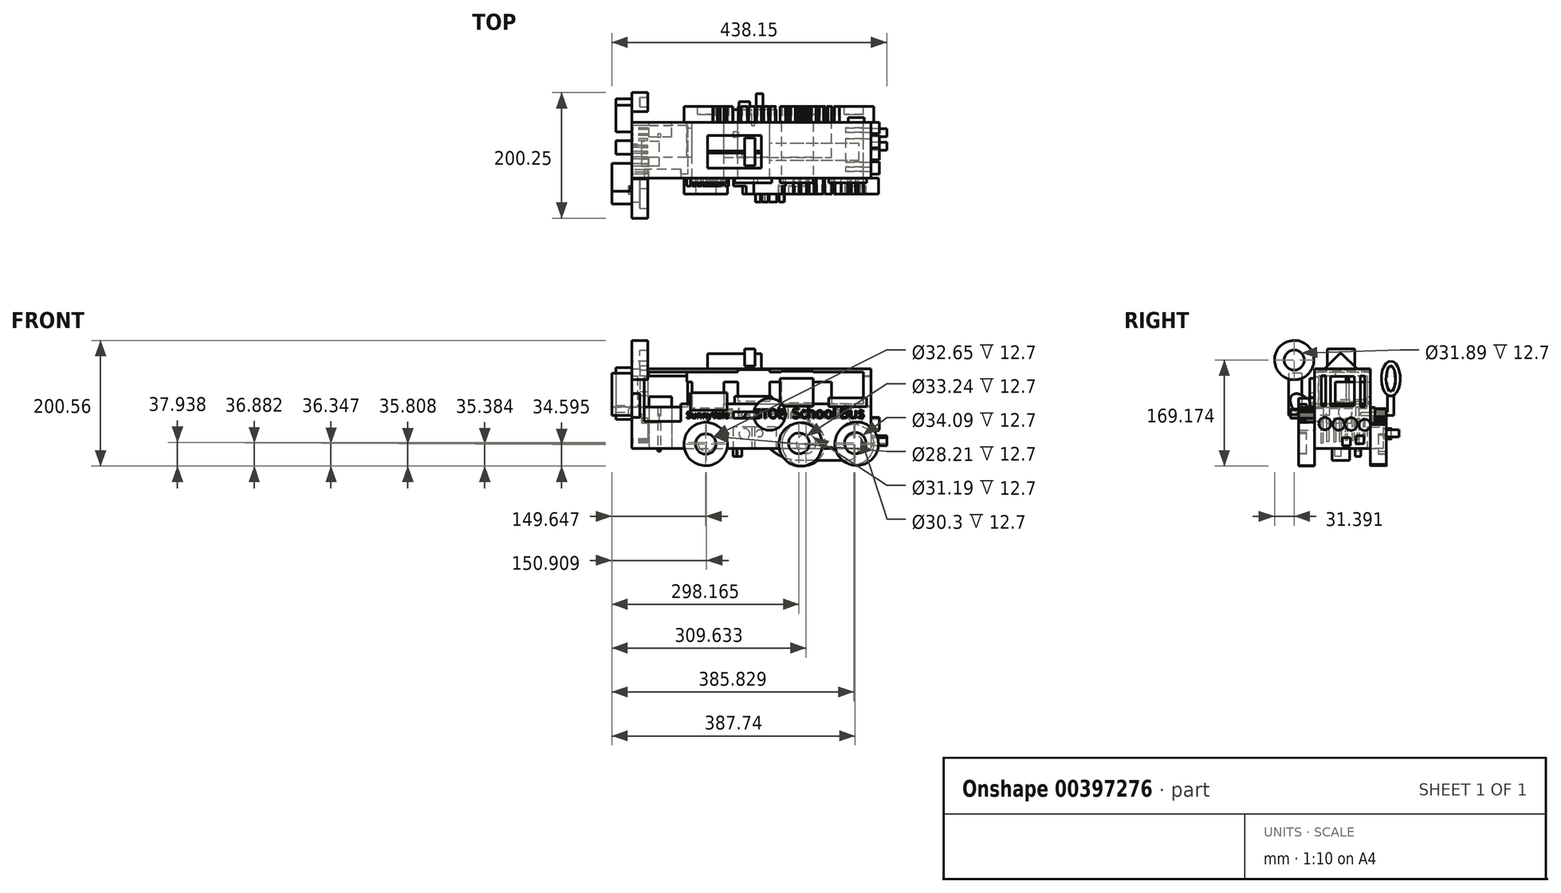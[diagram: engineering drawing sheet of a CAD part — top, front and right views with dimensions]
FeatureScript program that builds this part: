
annotation { "Feature Type Name" : "Feature", "Feature Type Description" : "" }
export const myFeature = defineFeature(function(context is Context, id is Id, definition is map)
    precondition{}
    {
        {
            var Q0;
            Q0=qCreatedBy(makeId("Front.planeOp"),FACE);
            var sketch = newSketch(context, id + "F0", { "sketchPlane" : qUnion([Q0])});
            skLineSegment(sketch, "E0.bottom", {"start": v(-219.61, 78.33) * mm, "end": v(161.39, 78.33) * mm});
            skLineSegment(sketch, "E0.top", {"start": v(-219.61, -48.19) * mm, "end": v(161.39, -48.19) * mm});
            skLineSegment(sketch, "E0.left", {"start": v(-219.61, 78.33) * mm, "end": v(-219.61, -48.19) * mm});
            skLineSegment(sketch, "E0.right", {"start": v(161.39, 78.33) * mm, "end": v(161.39, -48.19) * mm});
            skSolve(sketch);
        }
        {
            var Q0;
            Q0 = qSketchRegion(id + "F0", true);
            extrude(context, id + "F1", {"entities" : qUnion([Q0]), "depth" : 88.9 * mm});
        }
        {
            var Q0;
            Q0=makeQuery(id+"F1.opExtrude","CAP_FACE",FACE,{"disambiguationData":[OSD([sQuery(id+"F0.wireOp",EDGE,"E0.bottom"),sQuery(id+"F0.wireOp",EDGE,"E0.top"),sQuery(id+"F0.wireOp",EDGE,"E0.left"),sQuery(id+"F0.wireOp",EDGE,"E0.right")])],"isStart":true});
            var sketch = newSketch(context, id + "F2", { "sketchPlane" : qUnion([Q0])});
            skLineSegment(sketch, "E1.bottom", {"start": v(-149.58, 73.3) * mm, "end": v(-98.78, 73.3) * mm});
            skLineSegment(sketch, "E1.top", {"start": v(-149.58, 22.5) * mm, "end": v(-98.78, 22.5) * mm});
            skLineSegment(sketch, "E1.left", {"start": v(-149.58, 73.3) * mm, "end": v(-149.58, 22.5) * mm});
            skLineSegment(sketch, "E1.right", {"start": v(-98.78, 73.3) * mm, "end": v(-98.78, 22.5) * mm});
            skSolve(sketch);
        }
        {
            var Q0;
            Q0 = qSketchRegion(id + "F2", true);
            extrude(context, id + "F3", {"entities" : qUnion([Q0]), "operationType" : NewBodyOperationType.REMOVE, "oppositeDirection" : true, "depth" : 127 * mm});
        }
        {
            var Q0;
            Q0=makeQuery(id+"F1.opExtrude","CAP_FACE",FACE,{"disambiguationData":[OSD([sQuery(id+"F0.wireOp",EDGE,"E0.bottom"),sQuery(id+"F0.wireOp",EDGE,"E0.top"),sQuery(id+"F0.wireOp",EDGE,"E0.left"),sQuery(id+"F0.wireOp",EDGE,"E0.right")])],"isStart":false});
            var sketch = newSketch(context, id + "F4", { "sketchPlane" : qUnion([Q0])});
            skLineSegment(sketch, "E2.bottom", {"start": v(18.54, 74.81) * mm, "end": v(69.34, 74.81) * mm});
            skLineSegment(sketch, "E2.top", {"start": v(18.54, 24.01) * mm, "end": v(69.34, 24.01) * mm});
            skLineSegment(sketch, "E2.left", {"start": v(18.54, 74.81) * mm, "end": v(18.54, 24.01) * mm});
            skLineSegment(sketch, "E2.right", {"start": v(69.34, 74.81) * mm, "end": v(69.34, 24.01) * mm});
            skSolve(sketch);
        }
        {
            var Q0;
            Q0 = qSketchRegion(id + "F4", true);
            extrude(context, id + "F5", {"entities" : qUnion([Q0]), "operationType" : NewBodyOperationType.REMOVE, "oppositeDirection" : true, "depth" : 125.48 * mm});
        }
        {
            var Q0;
            Q0=makeQuery(id+"F1.opExtrude","CAP_FACE",FACE,{"disambiguationData":[OSD([sQuery(id+"F0.wireOp",EDGE,"E0.bottom"),sQuery(id+"F0.wireOp",EDGE,"E0.top"),sQuery(id+"F0.wireOp",EDGE,"E0.left"),sQuery(id+"F0.wireOp",EDGE,"E0.right")])],"isStart":true});
            var sketch = newSketch(context, id + "F6", { "sketchPlane" : qUnion([Q0])});
            skLineSegment(sketch, "E3.bottom", {"start": v(0, 76.96) * mm, "end": v(50.8, 76.96) * mm});
            skLineSegment(sketch, "E3.top", {"start": v(0, 26.16) * mm, "end": v(50.8, 26.16) * mm});
            skLineSegment(sketch, "E3.left", {"start": v(0, 76.96) * mm, "end": v(0, 26.16) * mm});
            skLineSegment(sketch, "E3.right", {"start": v(50.8, 76.96) * mm, "end": v(50.8, 26.16) * mm});
            skSolve(sketch);
        }
        {
            var Q0;
            Q0 = qSketchRegion(id + "F6", true);
            extrude(context, id + "F7", {"entities" : qUnion([Q0]), "operationType" : NewBodyOperationType.REMOVE, "oppositeDirection" : true, "depth" : 353.06 * mm});
        }
        {
            var Q0;
            Q0=makeQuery(id+"F1.opExtrude","CAP_FACE",FACE,{"disambiguationData":[OSD([sQuery(id+"F0.wireOp",EDGE,"E0.bottom"),sQuery(id+"F0.wireOp",EDGE,"E0.top"),sQuery(id+"F0.wireOp",EDGE,"E0.left"),sQuery(id+"F0.wireOp",EDGE,"E0.right")])],"isStart":true});
            var sketch = newSketch(context, id + "F8", { "sketchPlane" : qUnion([Q0])});
            skLineSegment(sketch, "E4.bottom", {"start": v(72.64, 66.26) * mm, "end": v(123.44, 66.26) * mm});
            skLineSegment(sketch, "E4.top", {"start": v(72.64, 15.46) * mm, "end": v(123.44, 15.46) * mm});
            skLineSegment(sketch, "E4.left", {"start": v(72.64, 66.26) * mm, "end": v(72.64, 15.46) * mm});
            skLineSegment(sketch, "E4.right", {"start": v(123.44, 66.26) * mm, "end": v(123.44, 15.46) * mm});
            skSolve(sketch);
        }
        {
            var Q0;
            Q0 = qSketchRegion(id + "F8", true);
            extrude(context, id + "F9", {"entities" : qUnion([Q0]), "operationType" : NewBodyOperationType.REMOVE, "oppositeDirection" : true, "depth" : 349 * mm});
        }
        {
            var Q0;
            Q0=makeQuery(id+"F1.opExtrude","CAP_FACE",FACE,{"disambiguationData":[OSD([sQuery(id+"F0.wireOp",EDGE,"E0.bottom"),sQuery(id+"F0.wireOp",EDGE,"E0.top"),sQuery(id+"F0.wireOp",EDGE,"E0.left"),sQuery(id+"F0.wireOp",EDGE,"E0.right")])],"isStart":true});
            var sketch = newSketch(context, id + "F10", { "sketchPlane" : qUnion([Q0])});
            skLineSegment(sketch, "E5.bottom", {"start": v(155.7, 34.18) * mm, "end": v(191.92, 34.18) * mm});
            skLineSegment(sketch, "E5.top", {"start": v(155.7, -48.19) * mm, "end": v(191.92, -48.19) * mm});
            skLineSegment(sketch, "E5.left", {"start": v(155.7, 34.18) * mm, "end": v(155.7, -48.19) * mm});
            skLineSegment(sketch, "E5.right", {"start": v(191.92, 34.18) * mm, "end": v(191.92, -48.19) * mm});
            skSolve(sketch);
        }
        {
            var Q0;
            Q0 = qSketchRegion(id + "F10", true);
            extrude(context, id + "F11", {"entities" : qUnion([Q0]), "operationType" : NewBodyOperationType.REMOVE, "oppositeDirection" : true, "depth" : 23.37 * mm});
        }
        {
            var Q0;
            Q0=makeQuery(id+"F1.opExtrude","SWEPT_FACE",FACE,{"disambiguationData":[OSD([sQuery(id+"F0.wireOp",EDGE,"E0.left")])]});
            var sketch = newSketch(context, id + "F12", { "sketchPlane" : qUnion([Q0])});
            skLineSegment(sketch, "E6.bottom", {"start": v(5.3, 67.15) * mm, "end": v(82.5, 67.15) * mm});
            skLineSegment(sketch, "E6.top", {"start": v(5.3, 17.89) * mm, "end": v(82.5, 17.89) * mm});
            skLineSegment(sketch, "E6.left", {"start": v(5.3, 67.15) * mm, "end": v(5.3, 17.89) * mm});
            skLineSegment(sketch, "E6.right", {"start": v(82.5, 67.15) * mm, "end": v(82.5, 17.89) * mm});
            skSolve(sketch);
        }
        {
            var Q0;
            Q0 = qSketchRegion(id + "F12", true);
            extrude(context, id + "F13", {"entities" : qUnion([Q0]), "operationType" : NewBodyOperationType.REMOVE, "oppositeDirection" : true, "depth" : 88.9 * mm});
        }
        {
            var Q0;
            Q0=makeQuery(id+"F1.opExtrude","CAP_FACE",FACE,{"disambiguationData":[OSD([sQuery(id+"F0.wireOp",EDGE,"E0.bottom"),sQuery(id+"F0.wireOp",EDGE,"E0.top"),sQuery(id+"F0.wireOp",EDGE,"E0.left"),sQuery(id+"F0.wireOp",EDGE,"E0.right")])],"isStart":true});
            var sketch = newSketch(context, id + "F14", { "sketchPlane" : qUnion([Q0])});
            skCircle(sketch, "E7", {"center": v(-134.47, -42.1) * mm, "radius": 31.77 * mm});
            skSolve(sketch);
        }
        {
            var Q0;
            Q0 = qSketchRegion(id + "F14", true);
            extrude(context, id + "F15", {"entities" : qUnion([Q0]), "operationType" : NewBodyOperationType.ADD, "depth" : 25.4 * mm});
        }
        {
            var Q0;
            Q0=makeQuery(id+"F1.opExtrude","CAP_FACE",FACE,{"disambiguationData":[OSD([sQuery(id+"F0.wireOp",EDGE,"E0.bottom"),sQuery(id+"F0.wireOp",EDGE,"E0.top"),sQuery(id+"F0.wireOp",EDGE,"E0.left"),sQuery(id+"F0.wireOp",EDGE,"E0.right")])],"isStart":true});
            var sketch = newSketch(context, id + "F16", { "sketchPlane" : qUnion([Q0])});
            skCircle(sketch, "E8", {"center": v(-54.26, -41.2) * mm, "radius": 34.6 * mm});
            skSolve(sketch);
        }
        {
            var Q0;
            Q0 = qSketchRegion(id + "F16", true);
            extrude(context, id + "F17", {"entities" : qUnion([Q0]), "operationType" : NewBodyOperationType.ADD, "depth" : 25.4 * mm});
        }
        {
            var Q0;
            Q0=makeQuery(id+"F1.opExtrude","CAP_FACE",FACE,{"disambiguationData":[OSD([sQuery(id+"F0.wireOp",EDGE,"E0.bottom"),sQuery(id+"F0.wireOp",EDGE,"E0.top"),sQuery(id+"F0.wireOp",EDGE,"E0.left"),sQuery(id+"F0.wireOp",EDGE,"E0.right")])],"isStart":true});
            var sketch = newSketch(context, id + "F18", { "sketchPlane" : qUnion([Q0])});
            skCircle(sketch, "E9", {"center": v(101.85, -41.13) * mm, "radius": 34.6 * mm});
            skSolve(sketch);
        }
        {
            var Q0;
            Q0 = qSketchRegion(id + "F18", true);
            extrude(context, id + "F19", {"entities" : qUnion([Q0]), "operationType" : NewBodyOperationType.ADD, "depth" : 25.4 * mm});
        }
        {
            var Q0;
            Q0=makeQuery(id+"F4.imprint","IMPRINT",FACE,{"disambiguationData":[TD([[makeQuery(id+"F4.imprint","IMPRINT",EDGE,{"derivedFrom":sQuery(id+"F4.wireOp",EDGE,"E2.bottom")}),1.0]])]});
            var sketch = newSketch(context, id + "F20", { "sketchPlane" : qUnion([Q0])});
            skCircle(sketch, "E10", {"center": v(138.8, -40.97) * mm, "radius": 34.6 * mm});
            skSolve(sketch);
        }
        {
            var Q0;
            Q0 = qSketchRegion(id + "F20", true);
            extrude(context, id + "F21", {"entities" : qUnion([Q0]), "operationType" : NewBodyOperationType.ADD, "depth" : 25.4 * mm});
        }
        {
            var Q0;
            Q0=makeQuery(id+"F4.imprint","IMPRINT",FACE,{"disambiguationData":[TD([[makeQuery(id+"F4.imprint","IMPRINT",EDGE,{"derivedFrom":sQuery(id+"F4.wireOp",EDGE,"E2.bottom")}),1.0]])]});
            var sketch = newSketch(context, id + "F22", { "sketchPlane" : qUnion([Q0])});
            skCircle(sketch, "E11", {"center": v(49.35, -42.1) * mm, "radius": 34.6 * mm});
            skSolve(sketch);
        }
        {
            var Q0;
            Q0 = qSketchRegion(id + "F22", true);
            extrude(context, id + "F23", {"entities" : qUnion([Q0]), "operationType" : NewBodyOperationType.ADD, "depth" : 25.4 * mm});
        }
        {
            var Q0;
            Q0=makeQuery(id+"F4.imprint","IMPRINT",FACE,{"disambiguationData":[TD([[makeQuery(id+"F4.imprint","IMPRINT",EDGE,{"derivedFrom":sQuery(id+"F4.wireOp",EDGE,"E2.bottom")}),1.0]])]});
            var sketch = newSketch(context, id + "F24", { "sketchPlane" : qUnion([Q0])});
            skCircle(sketch, "E12", {"center": v(-101.71, -41.32) * mm, "radius": 34.6 * mm});
            skSolve(sketch);
        }
        {
            var Q0;
            Q0 = qSketchRegion(id + "F24", true);
            extrude(context, id + "F25", {"entities" : qUnion([Q0]), "operationType" : NewBodyOperationType.ADD, "depth" : 25.4 * mm});
        }
        {
            var Q0;
            Q0=makeQuery(id+"F4.imprint","IMPRINT",FACE,{"disambiguationData":[TD([[makeQuery(id+"F4.imprint","IMPRINT",EDGE,{"derivedFrom":sQuery(id+"F4.wireOp",EDGE,"E2.bottom")}),1.0]])]});
            var sketch = newSketch(context, id + "F26", { "sketchPlane" : qUnion([Q0])});
            skLineSegment(sketch, "E13.bottom", {"start": v(-199.74, 65.16) * mm, "end": v(-141.38, 65.16) * mm});
            skLineSegment(sketch, "E13.top", {"start": v(-199.74, -5.59) * mm, "end": v(-141.38, -5.59) * mm});
            skLineSegment(sketch, "E13.left", {"start": v(-199.74, 65.16) * mm, "end": v(-199.74, -5.59) * mm});
            skLineSegment(sketch, "E13.right", {"start": v(-141.38, 65.16) * mm, "end": v(-141.38, -5.59) * mm});
            skSolve(sketch);
        }
        {
            var Q0;
            Q0 = qSketchRegion(id + "F26", true);
            extrude(context, id + "F27", {"entities" : qUnion([Q0]), "operationType" : NewBodyOperationType.REMOVE, "oppositeDirection" : true, "depth" : 13.97 * mm});
        }
        {
            var Q0;
            Q0=makeQuery(id+"F1.opExtrude","SWEPT_FACE",FACE,{"disambiguationData":[OSD([sQuery(id+"F0.wireOp",EDGE,"E0.bottom")])]});
            var sketch = newSketch(context, id + "F28", { "sketchPlane" : qUnion([Q0])});
            skLineSegment(sketch, "E14.bottom", {"start": v(-99.07, -74.11) * mm, "end": v(-13, -74.11) * mm});
            skLineSegment(sketch, "E14.top", {"start": v(-99.07, -20.3) * mm, "end": v(-13, -20.3) * mm});
            skLineSegment(sketch, "E14.left", {"start": v(-99.07, -74.11) * mm, "end": v(-99.07, -20.3) * mm});
            skLineSegment(sketch, "E14.right", {"start": v(-13, -74.11) * mm, "end": v(-13, -20.3) * mm});
            skSolve(sketch);
        }
        {
            var Q0;
            Q0 = qSketchRegion(id + "F28", true);
            extrude(context, id + "F29", {"entities" : qUnion([Q0]), "operationType" : NewBodyOperationType.ADD, "depth" : 24.64 * mm});
        }
        {
            var Q0;
            Q0=makeQuery(id+"F29.opExtrude","CAP_FACE",FACE,{"disambiguationData":[OSD([sQuery(id+"F28.wireOp",EDGE,"E14.bottom"),sQuery(id+"F28.wireOp",EDGE,"E14.top"),sQuery(id+"F28.wireOp",EDGE,"E14.left"),sQuery(id+"F28.wireOp",EDGE,"E14.right")])],"isStart":false});
            var sketch = newSketch(context, id + "F30", { "sketchPlane" : qUnion([Q0])});
            skLineSegment(sketch, "E15.bottom", {"start": v(-39.87, -68.95) * mm, "end": v(-23.5, -68.95) * mm});
            skLineSegment(sketch, "E15.top", {"start": v(-39.87, -24.8) * mm, "end": v(-23.5, -24.8) * mm});
            skLineSegment(sketch, "E15.left", {"start": v(-39.87, -68.95) * mm, "end": v(-39.87, -24.8) * mm});
            skLineSegment(sketch, "E15.right", {"start": v(-23.5, -68.95) * mm, "end": v(-23.5, -24.8) * mm});
            skSolve(sketch);
        }
        {
            var Q0;
            Q0 = qSketchRegion(id + "F30", true);
            extrude(context, id + "F31", {"entities" : qUnion([Q0]), "operationType" : NewBodyOperationType.ADD, "depth" : 7.62 * mm});
        }
        {
            var Q0;
            Q0=makeQuery(id+"F1.opExtrude","SWEPT_FACE",FACE,{"disambiguationData":[OSD([sQuery(id+"F0.wireOp",EDGE,"E0.right")])]});
            var sketch = newSketch(context, id + "F32", { "sketchPlane" : qUnion([Q0])});
            skLineSegment(sketch, "E16.bottom", {"start": v(-22.79, -27.9) * mm, "end": v(-10.09, -27.9) * mm});
            skLineSegment(sketch, "E16.top", {"start": v(-22.79, -40.6) * mm, "end": v(-10.09, -40.6) * mm});
            skLineSegment(sketch, "E16.left", {"start": v(-22.79, -27.9) * mm, "end": v(-22.79, -40.6) * mm});
            skLineSegment(sketch, "E16.right", {"start": v(-10.09, -27.9) * mm, "end": v(-10.09, -40.6) * mm});
            skSolve(sketch);
        }
        {
            var Q0;
            Q0 = qSketchRegion(id + "F32", true);
            extrude(context, id + "F33", {"entities" : qUnion([Q0]), "operationType" : NewBodyOperationType.ADD, "depth" : 25.4 * mm});
        }
        {
            var Q0;
            Q0=makeQuery(id+"F1.opExtrude","SWEPT_FACE",FACE,{"disambiguationData":[OSD([sQuery(id+"F0.wireOp",EDGE,"E0.right")])]});
            var sketch = newSketch(context, id + "F34", { "sketchPlane" : qUnion([Q0])});
            skPoint(sketch, "E17.firstSnap0", {"position": v(-44.45, -48.19) * mm});
            skLineSegment(sketch, "E17.bottom", {"start": v(-44.45, -31.5) * mm, "end": v(-31.75, -31.5) * mm});
            skLineSegment(sketch, "E17.top", {"start": v(-44.45, -44.2) * mm, "end": v(-31.75, -44.2) * mm});
            skLineSegment(sketch, "E17.left", {"start": v(-44.45, -31.5) * mm, "end": v(-44.45, -44.2) * mm});
            skLineSegment(sketch, "E17.right", {"start": v(-31.75, -31.5) * mm, "end": v(-31.75, -44.2) * mm});
            skSolve(sketch);
        }
        {
            var Q0;
            Q0 = qSketchRegion(id + "F34", true);
            extrude(context, id + "F35", {"entities" : qUnion([Q0]), "operationType" : NewBodyOperationType.ADD, "depth" : 25.4 * mm});
        }
        {
            var Q0;
            Q0=makeQuery(id+"F13.boolean.opBoolean","COPY",FACE,{"derivedFrom":makeQuery(id+"F13.opExtrude","CAP_FACE",FACE,{"disambiguationData":[OSD([sQuery(id+"F12.wireOp",EDGE,"E6.bottom"),sQuery(id+"F12.wireOp",EDGE,"E6.top"),sQuery(id+"F12.wireOp",EDGE,"E6.left"),sQuery(id+"F12.wireOp",EDGE,"E6.right")])],"isStart":false})});
            var sketch = newSketch(context, id + "F36", { "sketchPlane" : qUnion([Q0])});
            skLineSegment(sketch, "E18.bottom", {"start": v(9.47, 63.82) * mm, "end": v(71.4, 63.82) * mm});
            skLineSegment(sketch, "E18.top", {"start": v(9.47, 29.22) * mm, "end": v(71.4, 29.22) * mm});
            skLineSegment(sketch, "E18.left", {"start": v(9.47, 63.82) * mm, "end": v(9.47, 29.22) * mm});
            skLineSegment(sketch, "E18.right", {"start": v(71.4, 63.82) * mm, "end": v(71.4, 29.22) * mm});
            skSolve(sketch);
        }
        {
            var Q0;
            Q0 = qSketchRegion(id + "F36", true);
            extrude(context, id + "F37", {"entities" : qUnion([Q0]), "operationType" : NewBodyOperationType.REMOVE, "oppositeDirection" : true, "depth" : 25.4 * mm});
        }
        {
            var Q0;
            Q0=makeQuery(id+"F11.boolean.opBoolean","COPY",FACE,{"derivedFrom":makeQuery(id+"F11.opExtrude","CAP_FACE",FACE,{"disambiguationData":[OSD([sQuery(id+"F10.wireOp",EDGE,"E5.bottom"),sQuery(id+"F10.wireOp",EDGE,"E5.top"),sQuery(id+"F10.wireOp",EDGE,"E5.left"),sQuery(id+"F10.wireOp",EDGE,"E5.right")])],"isStart":false})});
            var sketch = newSketch(context, id + "F38", { "sketchPlane" : qUnion([Q0])});
            skLineSegment(sketch, "E19.bottom", {"start": v(173.8, 17.89) * mm, "end": v(178.4, 17.89) * mm});
            skLineSegment(sketch, "E19.top", {"start": v(173.8, -53.03) * mm, "end": v(178.4, -53.03) * mm});
            skLineSegment(sketch, "E19.left", {"start": v(173.8, 17.89) * mm, "end": v(173.8, -53.03) * mm});
            skLineSegment(sketch, "E19.right", {"start": v(178.4, 17.89) * mm, "end": v(178.4, -53.03) * mm});
            skSolve(sketch);
        }
        {
            var Q0;
            Q0 = qSketchRegion(id + "F38", true);
            extrude(context, id + "F39", {"entities" : qUnion([Q0]), "operationType" : NewBodyOperationType.ADD, "depth" : 5.08 * mm});
        }
        {
            var Q0;
            Q0=makeQuery(id+"F1.opExtrude","SWEPT_FACE",FACE,{"disambiguationData":[OSD([sQuery(id+"F0.wireOp",EDGE,"E0.left")])]});
            var sketch = newSketch(context, id + "F40", { "sketchPlane" : qUnion([Q0])});
            skLineSegment(sketch, "E20.bottom", {"start": v(34.5, 72.23) * mm, "end": v(38.68, 72.23) * mm});
            skLineSegment(sketch, "E20.top", {"start": v(34.5, 11.97) * mm, "end": v(38.68, 11.97) * mm});
            skLineSegment(sketch, "E20.left", {"start": v(34.5, 72.23) * mm, "end": v(34.5, 11.97) * mm});
            skLineSegment(sketch, "E20.right", {"start": v(38.68, 72.23) * mm, "end": v(38.68, 11.97) * mm});
            skSolve(sketch);
        }
        {
            var Q0;
            Q0 = qSketchRegion(id + "F40", true);
            extrude(context, id + "F41", {"entities" : qUnion([Q0]), "operationType" : NewBodyOperationType.ADD, "oppositeDirection" : true, "depth" : 9.14 * mm});
        }
        {
            var Q0;
            Q0=makeQuery(id+"F4.imprint","IMPRINT",FACE,{"disambiguationData":[TD([[makeQuery(id+"F4.imprint","IMPRINT",EDGE,{"derivedFrom":sQuery(id+"F4.wireOp",EDGE,"E2.bottom")}),1.0]])]});
            var sketch = newSketch(context, id + "F42", { "sketchPlane" : qUnion([Q0])});
            skLineSegment(sketch, "E21.bottom", {"start": v(-57.35, 0) * mm, "end": v(-25.01, 0) * mm});
            skLineSegment(sketch, "E21.top", {"start": v(-57.35, 9.97) * mm, "end": v(-25.01, 9.97) * mm});
            skLineSegment(sketch, "E21.left", {"start": v(-57.35, 0) * mm, "end": v(-57.35, 9.97) * mm});
            skLineSegment(sketch, "E21.right", {"start": v(-25.01, 0) * mm, "end": v(-25.01, 9.97) * mm});
            skSolve(sketch);
        }
        {
            var Q0;
            Q0 = qSketchRegion(id + "F42", true);
            extrude(context, id + "F43", {"entities" : qUnion([Q0]), "operationType" : NewBodyOperationType.ADD, "depth" : 25.4 * mm});
        }
        {
            var Q0;
            Q0=makeQuery(id+"F4.imprint","IMPRINT",FACE,{"disambiguationData":[TD([[makeQuery(id+"F4.imprint","IMPRINT",EDGE,{"derivedFrom":sQuery(id+"F4.wireOp",EDGE,"E2.bottom")}),1.0]])]});
            var sketch = newSketch(context, id + "F44", { "sketchPlane" : qUnion([Q0])});
            skCircle(sketch, "E22", {"center": v(0, 6.06) * mm, "radius": 25.45 * mm});
            skSolve(sketch);
        }
        {
            var Q0;
            Q0 = qSketchRegion(id + "F44", true);
            extrude(context, id + "F45", {"entities" : qUnion([Q0]), "operationType" : NewBodyOperationType.ADD, "depth" : 25.4 * mm});
        }
        {
            var Q0;
            Q0=makeQuery(id+"F41.boolean.opBoolean","MERGE",FACE,{"derivedFrom":[makeQuery(id+"F1.opExtrude","SWEPT_FACE",FACE,{"disambiguationData":[OSD([sQuery(id+"F0.wireOp",EDGE,"E0.left")])]}),makeQuery(id+"F41.opExtrude","CAP_FACE",FACE,{"disambiguationData":[OSD([sQuery(id+"F40.wireOp",EDGE,"E20.bottom"),sQuery(id+"F40.wireOp",EDGE,"E20.top"),sQuery(id+"F40.wireOp",EDGE,"E20.left"),sQuery(id+"F40.wireOp",EDGE,"E20.right")])],"isStart":true})]});
            var sketch = newSketch(context, id + "F46", { "sketchPlane" : qUnion([Q0])});
            skLineSegment(sketch, "E23.bottom", {"start": v(15.22, 3.97) * mm, "end": v(-35.58, 3.97) * mm});
            skLineSegment(sketch, "E23.top", {"start": v(15.22, 9.05) * mm, "end": v(-35.58, 9.05) * mm});
            skLineSegment(sketch, "E23.left", {"start": v(15.22, 3.97) * mm, "end": v(15.22, 9.05) * mm});
            skLineSegment(sketch, "E23.right", {"start": v(-35.58, 3.97) * mm, "end": v(-35.58, 9.05) * mm});
            skSolve(sketch);
        }
        {
            var Q0;
            Q0 = qSketchRegion(id + "F46", true);
            extrude(context, id + "F47", {"entities" : qUnion([Q0]), "operationType" : NewBodyOperationType.ADD, "depth" : 25.4 * mm});
        }
        {
            var Q0;
            Q0=makeQuery(id+"F47.opExtrude","CAP_FACE",FACE,{"disambiguationData":[OSD([sQuery(id+"F46.wireOp",EDGE,"E23.bottom"),sQuery(id+"F46.wireOp",EDGE,"E23.top"),sQuery(id+"F46.wireOp",EDGE,"E23.left"),sQuery(id+"F46.wireOp",EDGE,"E23.right")])],"isStart":false});
            var sketch = newSketch(context, id + "F48", { "sketchPlane" : qUnion([Q0])});
            skLineSegment(sketch, "E24.bottom", {"start": v(-37.55, 80.17) * mm, "end": v(-27.39, 80.17) * mm});
            skLineSegment(sketch, "E24.top", {"start": v(-37.55, 3.97) * mm, "end": v(-27.39, 3.97) * mm});
            skLineSegment(sketch, "E24.left", {"start": v(-37.55, 80.17) * mm, "end": v(-37.55, 3.97) * mm});
            skLineSegment(sketch, "E24.right", {"start": v(-27.39, 80.17) * mm, "end": v(-27.39, 3.97) * mm});
            skSolve(sketch);
        }
        {
            var Q0;
            Q0 = qSketchRegion(id + "F48", true);
            extrude(context, id + "F49", {"entities" : qUnion([Q0]), "operationType" : NewBodyOperationType.ADD, "oppositeDirection" : true, "depth" : 25.4 * mm});
        }
        {
            var Q0;
            Q0=makeQuery(id+"F49.boolean.opBoolean","MERGE",FACE,{"derivedFrom":[makeQuery(id+"F47.opExtrude","CAP_FACE",FACE,{"disambiguationData":[OSD([sQuery(id+"F46.wireOp",EDGE,"E23.bottom"),sQuery(id+"F46.wireOp",EDGE,"E23.top"),sQuery(id+"F46.wireOp",EDGE,"E23.left"),sQuery(id+"F46.wireOp",EDGE,"E23.right")])],"isStart":true}),makeQuery(id+"F49.opExtrude","CAP_FACE",FACE,{"disambiguationData":[OSD([sQuery(id+"F48.wireOp",EDGE,"E24.bottom"),sQuery(id+"F48.wireOp",EDGE,"E24.top"),sQuery(id+"F48.wireOp",EDGE,"E24.left"),sQuery(id+"F48.wireOp",EDGE,"E24.right")])],"isStart":false})]});
            var sketch = newSketch(context, id + "F50", { "sketchPlane" : qUnion([Q0])});
            skEllipse(sketch, "E25", {"center": v(32.47, 62.95) * mm, "majorRadius": 27.83 * mm, "minorRadius": 15.03 * mm, "majorAxis": v(0, 1)});
            skPoint(sketch, "E25.centerSnap0", {"position": v(32.47, 80.17) * mm});
            skSolve(sketch);
        }
        {
            var Q0;
            Q0 = qSketchRegion(id + "F50", true);
            extrude(context, id + "F51", {"entities" : qUnion([Q0]), "operationType" : NewBodyOperationType.ADD, "depth" : 25.4 * mm});
        }
        {
            var Q0;
            Q0=makeQuery(id+"F1.opExtrude","SWEPT_FACE",FACE,{"disambiguationData":[OSD([sQuery(id+"F0.wireOp",EDGE,"E0.top")])]});
            var sketch = newSketch(context, id + "F52", { "sketchPlane" : qUnion([Q0])});
            skLineSegment(sketch, "E26.bottom", {"start": v(142.29, 61.1) * mm, "end": v(0, 61.1) * mm});
            skLineSegment(sketch, "E26.top", {"start": v(142.29, 33.4) * mm, "end": v(0, 33.4) * mm});
            skLineSegment(sketch, "E26.left", {"start": v(142.29, 61.1) * mm, "end": v(142.29, 33.4) * mm});
            skLineSegment(sketch, "E26.right", {"start": v(0, 61.1) * mm, "end": v(0, 33.4) * mm});
            skSolve(sketch);
        }
        {
            var Q0;
            Q0 = qSketchRegion(id + "F52", true);
            extrude(context, id + "F53", {"entities" : qUnion([Q0]), "operationType" : NewBodyOperationType.ADD, "depth" : 19.05 * mm});
        }
        {
            var Q0;
            Q0=makeQuery(id+"F53.opExtrude","CAP_EDGE",EDGE,{"disambiguationData":[OSD([sQuery(id+"F52.wireOp",EDGE,"E26.left")])],"isStart":false});
            fillet(context, id + "F54", {"entities" : qUnion([Q0]), "radius" : 18.4 * mm, "tangentPropagation" : true, "allowEdgeOverflow" : false});
        }
        {
            var Q0;
            Q0=makeQuery(id+"F53.opExtrude","CAP_EDGE",EDGE,{"disambiguationData":[OSD([sQuery(id+"F52.wireOp",EDGE,"E26.right")])],"isStart":false});
            fillet(context, id + "F55", {"entities" : qUnion([Q0]), "radius" : 69.9 * mm, "tangentPropagation" : true, "allowEdgeOverflow" : false});
        }
        {
            var Q0;
            Q0=makeQuery(id+"F1.opExtrude","SWEPT_FACE",FACE,{"disambiguationData":[OSD([sQuery(id+"F0.wireOp",EDGE,"E0.right")])]});
            var sketch = newSketch(context, id + "F56", { "sketchPlane" : qUnion([Q0])});
            skCircle(sketch, "E27", {"center": v(-72.52, -8.72) * mm, "radius": 9.86 * mm});
            skCircle(sketch, "E28", {"center": v(-50.6, -9.9) * mm, "radius": 9.4 * mm});
            skCircle(sketch, "E29", {"center": v(-30.5, -9.65) * mm, "radius": 10.03 * mm});
            skCircle(sketch, "E30", {"center": v(-9.12, -10.9) * mm, "radius": 9 * mm});
            skSolve(sketch);
        }
        {
            var Q0;
            Q0 = qSketchRegion(id + "F56", true);
            extrude(context, id + "F57", {"entities" : qUnion([Q0]), "operationType" : NewBodyOperationType.ADD, "depth" : 13.72 * mm});
        }
        {
            var Q0;
            Q0=makeQuery(id+"F29.opExtrude","CAP_EDGE",EDGE,{"disambiguationData":[OSD([sQuery(id+"F28.wireOp",EDGE,"E14.bottom")])],"isStart":false});
            chamfer(context, id + "F58", {"entities" : qUnion([Q0]), "width" : 25.4 * mm, "tangentPropagation" : true});
        }
        {
            var Q0;
            Q0=makeQuery(id+"F29.opExtrude","CAP_EDGE",EDGE,{"disambiguationData":[OSD([sQuery(id+"F28.wireOp",EDGE,"E14.top")])],"isStart":false});
            chamfer(context, id + "F59", {"entities" : qUnion([Q0]), "width" : 25.4 * mm, "tangentPropagation" : true});
        }
        {
            var Q0;
            Q0=makeQuery(id+"F1.opExtrude","SWEPT_FACE",FACE,{"disambiguationData":[OSD([sQuery(id+"F0.wireOp",EDGE,"E0.right")])]});
            var sketch = newSketch(context, id + "F60", { "sketchPlane" : qUnion([Q0])});
            skLineSegment(sketch, "E31.bottom", {"start": v(-78.08, 67.76) * mm, "end": v(-71.03, 67.76) * mm});
            skLineSegment(sketch, "E31.top", {"start": v(-78.08, 19.57) * mm, "end": v(-71.03, 19.57) * mm});
            skLineSegment(sketch, "E31.left", {"start": v(-78.08, 67.76) * mm, "end": v(-78.08, 19.57) * mm});
            skLineSegment(sketch, "E31.right", {"start": v(-71.03, 67.76) * mm, "end": v(-71.03, 19.57) * mm});
            skLineSegment(sketch, "E32.bottom", {"start": v(-63.33, 66.55) * mm, "end": v(-25.82, 66.55) * mm});
            skLineSegment(sketch, "E32.top", {"start": v(-63.33, 19.2) * mm, "end": v(-25.82, 19.2) * mm});
            skLineSegment(sketch, "E32.left", {"start": v(-63.33, 66.55) * mm, "end": v(-63.33, 19.2) * mm});
            skLineSegment(sketch, "E32.right", {"start": v(-25.82, 66.55) * mm, "end": v(-25.82, 19.2) * mm});
            skLineSegment(sketch, "E33.bottom", {"start": v(-16.2, 67.08) * mm, "end": v(-9.16, 67.08) * mm});
            skLineSegment(sketch, "E33.top", {"start": v(-16.2, 18.43) * mm, "end": v(-9.16, 18.43) * mm});
            skLineSegment(sketch, "E33.left", {"start": v(-16.2, 67.08) * mm, "end": v(-16.2, 18.43) * mm});
            skLineSegment(sketch, "E33.right", {"start": v(-9.16, 67.08) * mm, "end": v(-9.16, 18.43) * mm});
            skSolve(sketch);
        }
        {
            var Q0;
            Q0 = qSketchRegion(id + "F60", true);
            extrude(context, id + "F61", {"entities" : qUnion([Q0]), "operationType" : NewBodyOperationType.REMOVE, "oppositeDirection" : true, "depth" : 40.64 * mm});
        }
        {
            var Q0;
            Q0=makeQuery(id+"F41.boolean.opBoolean","MERGE",FACE,{"derivedFrom":[makeQuery(id+"F1.opExtrude","SWEPT_FACE",FACE,{"disambiguationData":[OSD([sQuery(id+"F0.wireOp",EDGE,"E0.left")])]}),makeQuery(id+"F41.opExtrude","CAP_FACE",FACE,{"disambiguationData":[OSD([sQuery(id+"F40.wireOp",EDGE,"E20.bottom"),sQuery(id+"F40.wireOp",EDGE,"E20.top"),sQuery(id+"F40.wireOp",EDGE,"E20.left"),sQuery(id+"F40.wireOp",EDGE,"E20.right")])],"isStart":true})]});
            var sketch = newSketch(context, id + "F62", { "sketchPlane" : qUnion([Q0])});
            skLineSegment(sketch, "E34.bottom", {"start": v(11.51, 0) * mm, "end": v(8.72, 0) * mm});
            skLineSegment(sketch, "E34.top", {"start": v(11.51, -33.03) * mm, "end": v(8.72, -33.03) * mm});
            skLineSegment(sketch, "E34.left", {"start": v(11.51, 0) * mm, "end": v(11.51, -33.03) * mm});
            skLineSegment(sketch, "E34.right", {"start": v(8.72, 0) * mm, "end": v(8.72, -33.03) * mm});
            skLineSegment(sketch, "E35.bottom", {"start": v(21.03, 0) * mm, "end": v(18.24, 0) * mm});
            skLineSegment(sketch, "E35.top", {"start": v(21.03, -33.8) * mm, "end": v(18.24, -33.8) * mm});
            skLineSegment(sketch, "E35.left", {"start": v(21.03, 0) * mm, "end": v(21.03, -33.8) * mm});
            skLineSegment(sketch, "E35.right", {"start": v(18.24, 0) * mm, "end": v(18.24, -33.8) * mm});
            skLineSegment(sketch, "E36.bottom", {"start": v(29.12, 0) * mm, "end": v(26.33, 0) * mm});
            skLineSegment(sketch, "E36.top", {"start": v(29.12, -35.04) * mm, "end": v(26.33, -35.04) * mm});
            skLineSegment(sketch, "E36.left", {"start": v(29.12, 0) * mm, "end": v(29.12, -35.04) * mm});
            skLineSegment(sketch, "E36.right", {"start": v(26.33, 0) * mm, "end": v(26.33, -35.04) * mm});
            skLineSegment(sketch, "E37.bottom", {"start": v(40.07, 0) * mm, "end": v(36.8, 0) * mm});
            skLineSegment(sketch, "E37.top", {"start": v(40.07, -35.32) * mm, "end": v(36.8, -35.32) * mm});
            skLineSegment(sketch, "E37.left", {"start": v(40.07, 0) * mm, "end": v(40.07, -35.32) * mm});
            skLineSegment(sketch, "E37.right", {"start": v(36.8, 0) * mm, "end": v(36.8, -35.32) * mm});
            skLineSegment(sketch, "E38.bottom", {"start": v(49.59, 0) * mm, "end": v(46.32, 0) * mm});
            skLineSegment(sketch, "E38.top", {"start": v(49.59, -37) * mm, "end": v(46.32, -37) * mm});
            skLineSegment(sketch, "E38.left", {"start": v(49.59, 0) * mm, "end": v(49.59, -37) * mm});
            skLineSegment(sketch, "E38.right", {"start": v(46.32, 0) * mm, "end": v(46.32, -37) * mm});
            skLineSegment(sketch, "E39.bottom", {"start": v(58.63, 0) * mm, "end": v(55.37, 0) * mm});
            skLineSegment(sketch, "E39.top", {"start": v(58.63, -37.77) * mm, "end": v(55.37, -37.77) * mm});
            skLineSegment(sketch, "E39.left", {"start": v(58.63, 0) * mm, "end": v(58.63, -37.77) * mm});
            skLineSegment(sketch, "E39.right", {"start": v(55.37, 0) * mm, "end": v(55.37, -37.77) * mm});
            skLineSegment(sketch, "E40.bottom", {"start": v(70.05, 0) * mm, "end": v(66.32, 0) * mm});
            skLineSegment(sketch, "E40.top", {"start": v(70.05, -37.1) * mm, "end": v(66.32, -37.1) * mm});
            skLineSegment(sketch, "E40.left", {"start": v(70.05, 0) * mm, "end": v(70.05, -37.1) * mm});
            skLineSegment(sketch, "E40.right", {"start": v(66.32, 0) * mm, "end": v(66.32, -37.1) * mm});
            skLineSegment(sketch, "E41.bottom", {"start": v(79.1, 0) * mm, "end": v(75.84, 0) * mm});
            skLineSegment(sketch, "E41.top", {"start": v(79.1, -39.26) * mm, "end": v(75.84, -39.26) * mm});
            skLineSegment(sketch, "E41.left", {"start": v(79.1, 0) * mm, "end": v(79.1, -39.26) * mm});
            skLineSegment(sketch, "E41.right", {"start": v(75.84, 0) * mm, "end": v(75.84, -39.26) * mm});
            skSolve(sketch);
        }
        {
            var Q0;
            Q0 = qSketchRegion(id + "F62", true);
            extrude(context, id + "F63", {"entities" : qUnion([Q0]), "operationType" : NewBodyOperationType.REMOVE, "oppositeDirection" : true, "depth" : 25.4 * mm});
        }
        {
            var Q0;
            Q0=makeQuery(id+"F41.boolean.opBoolean","MERGE",FACE,{"derivedFrom":[makeQuery(id+"F1.opExtrude","SWEPT_FACE",FACE,{"disambiguationData":[OSD([sQuery(id+"F0.wireOp",EDGE,"E0.left")])]}),makeQuery(id+"F41.opExtrude","CAP_FACE",FACE,{"disambiguationData":[OSD([sQuery(id+"F40.wireOp",EDGE,"E20.bottom"),sQuery(id+"F40.wireOp",EDGE,"E20.top"),sQuery(id+"F40.wireOp",EDGE,"E20.left"),sQuery(id+"F40.wireOp",EDGE,"E20.right")])],"isStart":true})]});
            var sketch = newSketch(context, id + "F64", { "sketchPlane" : qUnion([Q0])});
            skCircle(sketch, "E42", {"center": v(40.07, 8.88) * mm, "radius": 10.95 * mm});
            skSolve(sketch);
        }
        {
            var Q0;
            Q0 = qSketchRegion(id + "F64", true);
            extrude(context, id + "F65", {"entities" : qUnion([Q0]), "operationType" : NewBodyOperationType.ADD, "depth" : 25.4 * mm});
        }
        {
            var Q0;
            Q0=makeQuery(id+"F1.opExtrude","CAP_FACE",FACE,{"disambiguationData":[OSD([sQuery(id+"F0.wireOp",EDGE,"E0.bottom"),sQuery(id+"F0.wireOp",EDGE,"E0.top"),sQuery(id+"F0.wireOp",EDGE,"E0.left"),sQuery(id+"F0.wireOp",EDGE,"E0.right")])],"isStart":true});
            var sketch = newSketch(context, id + "F66", { "sketchPlane" : qUnion([Q0])});
            skText(sketch, "E43", { "text": "SunnyVale School Bus", "fontName": "OpenSans-Regular.ttf"});
            const initialGuessF66  = {"E43": [-0.11263, 0, 1, 0, 0.01437]};
            skSetInitialGuess(sketch, initialGuessF66);
            skSolve(sketch);
        }
        {
            var Q0;
            Q0 = qSketchRegion(id + "F66", true);
            extrude(context, id + "F67", {"entities" : qUnion([Q0]), "operationType" : NewBodyOperationType.ADD, "depth" : 25.4 * mm});
        }
        {
            var Q0;
            Q0=makeQuery(id+"F4.imprint","IMPRINT",FACE,{"disambiguationData":[TD([[makeQuery(id+"F4.imprint","IMPRINT",EDGE,{"derivedFrom":sQuery(id+"F4.wireOp",EDGE,"E2.bottom")}),1.0]])]});
            var sketch = newSketch(context, id + "F68", { "sketchPlane" : qUnion([Q0])});
            skText(sketch, "E44", { "text": "SunnyVale", "fontName": "OpenSans-Regular.ttf"});
            const initialGuessF68  = {"E44": [-0.13246, 0, 1, 0, 0.01004]};
            skSetInitialGuess(sketch, initialGuessF68);
            skSolve(sketch);
        }
        {
            var Q0;
            Q0 = qSketchRegion(id + "F68", true);
            extrude(context, id + "F69", {"entities" : qUnion([Q0]), "operationType" : NewBodyOperationType.ADD, "depth" : 12.7 * mm});
        }
        {
            var Q0;
            Q0=makeQuery(id+"F4.imprint","IMPRINT",FACE,{"disambiguationData":[TD([[makeQuery(id+"F4.imprint","IMPRINT",EDGE,{"derivedFrom":sQuery(id+"F4.wireOp",EDGE,"E2.bottom")}),1.0]])]});
            var sketch = newSketch(context, id + "F70", { "sketchPlane" : qUnion([Q0])});
            skText(sketch, "E45", { "text": "School Bus", "fontName": "OpenSans-Regular.ttf"});
            const initialGuessF70  = {"E45": [0.03634, 0, 1, 0, 0.0162]};
            skSetInitialGuess(sketch, initialGuessF70);
            skSolve(sketch);
        }
        {
            var Q0;
            Q0 = qSketchRegion(id + "F70", true);
            extrude(context, id + "F71", {"entities" : qUnion([Q0]), "operationType" : NewBodyOperationType.ADD, "depth" : 25.4 * mm});
        }
        {
            var Q0;
            Q0=makeQuery(id+"F45.boolean.opBoolean","MERGE",FACE,{"derivedFrom":[makeQuery(id+"F43.opExtrude","CAP_FACE",FACE,{"disambiguationData":[OSD([sQuery(id+"F42.wireOp",EDGE,"E21.bottom"),sQuery(id+"F42.wireOp",EDGE,"E21.top"),sQuery(id+"F42.wireOp",EDGE,"E21.left"),sQuery(id+"F42.wireOp",EDGE,"E21.right")])],"isStart":false}),makeQuery(id+"F45.opExtrude","CAP_FACE",FACE,{"disambiguationData":[OSD([sQuery(id+"F44.wireOp",EDGE,"E22")])],"isStart":false})]});
            var sketch = newSketch(context, id + "F72", { "sketchPlane" : qUnion([Q0])});
            skText(sketch, "E46", { "text": "STOP", "fontName": "OpenSans-Regular.ttf"});
            const initialGuessF72  = {"E46": [-0.02352, 0, 1, 0, 0.014]};
            skSetInitialGuess(sketch, initialGuessF72);
            skSolve(sketch);
        }
        {
            var Q0;
            Q0 = qSketchRegion(id + "F72", true);
            extrude(context, id + "F73", {"entities" : qUnion([Q0]), "operationType" : NewBodyOperationType.ADD, "depth" : 12.7 * mm});
        }
        {
            var Q0;
            Q0=makeQuery(id+"F41.boolean.opBoolean","MERGE",FACE,{"derivedFrom":[makeQuery(id+"F1.opExtrude","SWEPT_FACE",FACE,{"disambiguationData":[OSD([sQuery(id+"F0.wireOp",EDGE,"E0.left")])]}),makeQuery(id+"F41.opExtrude","CAP_FACE",FACE,{"disambiguationData":[OSD([sQuery(id+"F40.wireOp",EDGE,"E20.bottom"),sQuery(id+"F40.wireOp",EDGE,"E20.top"),sQuery(id+"F40.wireOp",EDGE,"E20.left"),sQuery(id+"F40.wireOp",EDGE,"E20.right")])],"isStart":true})]});
            var sketch = newSketch(context, id + "F74", { "sketchPlane" : qUnion([Q0])});
            skLineSegment(sketch, "E47.bottom", {"start": v(65.4, 17.89) * mm, "end": v(130.36, 17.89) * mm});
            skLineSegment(sketch, "E47.top", {"start": v(65.4, 4.55) * mm, "end": v(130.36, 4.55) * mm});
            skLineSegment(sketch, "E47.left", {"start": v(65.4, 17.89) * mm, "end": v(65.4, 4.55) * mm});
            skLineSegment(sketch, "E47.right", {"start": v(130.36, 17.89) * mm, "end": v(130.36, 4.55) * mm});
            skSolve(sketch);
        }
        {
            var Q0;
            Q0 = qSketchRegion(id + "F74", true);
            extrude(context, id + "F75", {"entities" : qUnion([Q0]), "operationType" : NewBodyOperationType.ADD, "depth" : 31.75 * mm});
        }
        {
            var Q0;
            Q0=makeQuery(id+"F75.boolean.opBoolean","MERGE",FACE,{"derivedFrom":[makeQuery(id+"F39.boolean.opBoolean","MERGE",FACE,{"derivedFrom":[makeQuery(id+"F13.boolean.opBoolean","COPY",FACE,{"derivedFrom":makeQuery(id+"F13.opExtrude","SWEPT_FACE",FACE,{"disambiguationData":[OSD([sQuery(id+"F12.wireOp",EDGE,"E6.top")])]})}),makeQuery(id+"F39.opExtrude","SWEPT_FACE",FACE,{"disambiguationData":[OSD([sQuery(id+"F38.wireOp",EDGE,"E19.bottom")])]})]}),makeQuery(id+"F75.opExtrude","SWEPT_FACE",FACE,{"disambiguationData":[OSD([sQuery(id+"F74.wireOp",EDGE,"E47.bottom")])]})]});
            var sketch = newSketch(context, id + "F76", { "sketchPlane" : qUnion([Q0])});
            skLineSegment(sketch, "E48.bottom", {"start": v(-219.61, -109.63) * mm, "end": v(-251.36, -109.63) * mm});
            skLineSegment(sketch, "E48.top", {"start": v(-219.61, -130.36) * mm, "end": v(-251.36, -130.36) * mm});
            skLineSegment(sketch, "E48.left", {"start": v(-219.61, -109.63) * mm, "end": v(-219.61, -130.36) * mm});
            skLineSegment(sketch, "E48.right", {"start": v(-251.36, -109.63) * mm, "end": v(-251.36, -130.36) * mm});
            skSolve(sketch);
        }
        {
            var Q0;
            Q0 = qSketchRegion(id + "F76", true);
            extrude(context, id + "F77", {"entities" : qUnion([Q0]), "operationType" : NewBodyOperationType.ADD, "depth" : 53.6 * mm});
        }
        {
            var Q0;
            Q0=makeQuery(id+"F77.boolean.opBoolean","MERGE",FACE,{"derivedFrom":[makeQuery(id+"F75.opExtrude","CAP_FACE",FACE,{"disambiguationData":[OSD([sQuery(id+"F74.wireOp",EDGE,"E47.bottom"),sQuery(id+"F74.wireOp",EDGE,"E47.top"),sQuery(id+"F74.wireOp",EDGE,"E47.left"),sQuery(id+"F74.wireOp",EDGE,"E47.right")])],"isStart":true}),makeQuery(id+"F77.opExtrude","SWEPT_FACE",FACE,{"disambiguationData":[OSD([sQuery(id+"F76.wireOp",EDGE,"E48.left")])]})]});
            var sketch = newSketch(context, id + "F78", { "sketchPlane" : qUnion([Q0])});
            skCircle(sketch, "E49", {"center": v(-121.37, 92.47) * mm, "radius": 31.39 * mm});
            skSolve(sketch);
        }
        {
            var Q0;
            Q0 = qSketchRegion(id + "F78", true);
            extrude(context, id + "F79", {"entities" : qUnion([Q0]), "operationType" : NewBodyOperationType.ADD, "depth" : 25.4 * mm});
        }
        {
            var Q0;
            Q0=makeQuery(id+"F25.opExtrude","CAP_FACE",FACE,{"disambiguationData":[OSD([sQuery(id+"F24.wireOp",EDGE,"E12")])],"isStart":false});
            var sketch = newSketch(context, id + "F80", { "sketchPlane" : qUnion([Q0])});
            skCircle(sketch, "E50", {"center": v(-101.71, -41.32) * mm, "radius": 16.32 * mm});
            skCircle(sketch, "E51", {"center": v(46.8, -40.35) * mm, "radius": 16.62 * mm});
            skCircle(sketch, "E52", {"center": v(136.38, -39.82) * mm, "radius": 17.05 * mm});
            skCircle(sketch, "E53", {"center": v(-211.34, 8.74) * mm, "radius": 14.05 * mm});
            skCircle(sketch, "E54", {"center": v(-52.98, 11.77) * mm, "radius": 15.6 * mm});
            skCircle(sketch, "E55", {"center": v(27.13, 10.92) * mm, "radius": 13.55 * mm});
            skSolve(sketch);
        }
        {
            var Q0;
            Q0 = qSketchRegion(id + "F80", true);
            extrude(context, id + "F81", {"entities" : qUnion([Q0]), "operationType" : NewBodyOperationType.REMOVE, "oppositeDirection" : true, "depth" : 12.7 * mm});
        }
        {
            var Q0;
            Q0=makeQuery(id+"F15.opExtrude","CAP_FACE",FACE,{"disambiguationData":[OSD([sQuery(id+"F14.wireOp",EDGE,"E7")])],"isStart":false});
            var sketch = newSketch(context, id + "F82", { "sketchPlane" : qUnion([Q0])});
            skCircle(sketch, "E56", {"center": v(-134.47, -42.1) * mm, "radius": 15.15 * mm});
            skCircle(sketch, "E57", {"center": v(-58.27, -40.9) * mm, "radius": 15.6 * mm});
            skCircle(sketch, "E58", {"center": v(100.45, -38.76) * mm, "radius": 14.1 * mm});
            skSolve(sketch);
        }
        {
            var Q0;
            Q0 = qSketchRegion(id + "F82", true);
            extrude(context, id + "F83", {"entities" : qUnion([Q0]), "operationType" : NewBodyOperationType.REMOVE, "oppositeDirection" : true, "depth" : 12.7 * mm});
        }
        {
            var Q0;
            {var subQ0=sQuery(id+"F0.wireOp",EDGE,"E0.left");var subQ1=sQuery(id+"F0.wireOp",EDGE,"E0.top");var subQ2=sQuery(id+"F0.wireOp",EDGE,"E0.bottom");var subQ6=sQuery(id+"F0.wireOp",EDGE,"E0.right");Q0=makeQuery(id+"F67.boolean.opBoolean","SPLIT",FACE,{"disambiguationData":[TD([makeQuery(id+"F1.opExtrude","SWEPT_FACE",FACE,{"disambiguationData":[OSD([subQ2])]})])],"derivedFrom":makeQuery(id+"F1.opExtrude","CAP_FACE",FACE,{"disambiguationData":[OSD([subQ2,subQ1,subQ0,subQ6])],"isStart":true})});}
            var sketch = newSketch(context, id + "F84", { "sketchPlane" : qUnion([Q0])});
            skLineSegment(sketch, "E59.bottom", {"start": v(-10.72, -14.1) * mm, "end": v(57.97, -14.1) * mm});
            skLineSegment(sketch, "E59.top", {"start": v(-10.72, -48.19) * mm, "end": v(57.97, -48.19) * mm});
            skLineSegment(sketch, "E59.left", {"start": v(-10.72, -14.1) * mm, "end": v(-10.72, -48.19) * mm});
            skLineSegment(sketch, "E59.right", {"start": v(57.97, -14.1) * mm, "end": v(57.97, -48.19) * mm});
            skSolve(sketch);
        }
        {
            var Q0;
            Q0 = qSketchRegion(id + "F84", true);
            extrude(context, id + "F85", {"entities" : qUnion([Q0]), "operationType" : NewBodyOperationType.ADD, "depth" : 20.32 * mm});
        }
        {
            var Q0;
            Q0=makeQuery(id+"F85.opExtrude","CAP_FACE",FACE,{"disambiguationData":[OSD([sQuery(id+"F84.wireOp",EDGE,"E59.bottom"),sQuery(id+"F84.wireOp",EDGE,"E59.top"),sQuery(id+"F84.wireOp",EDGE,"E59.left"),sQuery(id+"F84.wireOp",EDGE,"E59.right")])],"isStart":false});
            var sketch = newSketch(context, id + "F86", { "sketchPlane" : qUnion([Q0])});
            skCircle(sketch, "E60", {"center": v(40.02, -25.03) * mm, "radius": 8.46 * mm});
            skSolve(sketch);
        }
        {
            var Q0;
            Q0 = qSketchRegion(id + "F86", true);
            extrude(context, id + "F87", {"entities" : qUnion([Q0]), "operationType" : NewBodyOperationType.ADD, "depth" : 12.7 * mm});
        }
        {
            var Q0;
            Q0=makeQuery(id+"F4.imprint","IMPRINT",FACE,{"disambiguationData":[TD([[makeQuery(id+"F4.imprint","IMPRINT",EDGE,{"derivedFrom":sQuery(id+"F4.wireOp",EDGE,"E2.bottom")}),1.0]])]});
            var sketch = newSketch(context, id + "F88", { "sketchPlane" : qUnion([Q0])});
            skLineSegment(sketch, "E61.bottom", {"start": v(-126.16, 40.47) * mm, "end": v(-67.63, 40.47) * mm});
            skLineSegment(sketch, "E61.top", {"start": v(-126.16, 12.28) * mm, "end": v(-67.63, 12.28) * mm});
            skLineSegment(sketch, "E61.left", {"start": v(-126.16, 40.47) * mm, "end": v(-126.16, 12.28) * mm});
            skLineSegment(sketch, "E61.right", {"start": v(-67.63, 40.47) * mm, "end": v(-67.63, 12.28) * mm});
            skLineSegment(sketch, "E62.bottom", {"start": v(-55.72, 34.86) * mm, "end": v(3.5, 34.86) * mm});
            skLineSegment(sketch, "E62.top", {"start": v(-55.72, 22.98) * mm, "end": v(3.5, 22.98) * mm});
            skLineSegment(sketch, "E62.left", {"start": v(-55.72, 34.86) * mm, "end": v(-55.72, 22.98) * mm});
            skLineSegment(sketch, "E62.right", {"start": v(3.5, 34.86) * mm, "end": v(3.5, 22.98) * mm});
            skLineSegment(sketch, "E63.bottom", {"start": v(16.9, 63.06) * mm, "end": v(69.5, 63.06) * mm});
            skLineSegment(sketch, "E63.top", {"start": v(16.9, 19.15) * mm, "end": v(69.5, 19.15) * mm});
            skLineSegment(sketch, "E63.left", {"start": v(16.9, 63.06) * mm, "end": v(16.9, 19.15) * mm});
            skLineSegment(sketch, "E63.right", {"start": v(69.5, 63.06) * mm, "end": v(69.5, 19.15) * mm});
            skLineSegment(sketch, "E64.bottom", {"start": v(93.95, 32.07) * mm, "end": v(154.52, 32.07) * mm});
            skLineSegment(sketch, "E64.top", {"start": v(93.95, 18.35) * mm, "end": v(154.52, 18.35) * mm});
            skLineSegment(sketch, "E64.left", {"start": v(93.95, 32.07) * mm, "end": v(93.95, 18.35) * mm});
            skLineSegment(sketch, "E64.right", {"start": v(154.52, 32.07) * mm, "end": v(154.52, 18.35) * mm});
            skSolve(sketch);
        }
        {
            var Q0;
            Q0 = qSketchRegion(id + "F88", true);
            extrude(context, id + "F89", {"entities" : qUnion([Q0]), "operationType" : NewBodyOperationType.ADD, "depth" : 7.62 * mm});
        }
        {
            var Q0;
            {var subQ0=sQuery(id+"F0.wireOp",EDGE,"E0.left");var subQ1=sQuery(id+"F0.wireOp",EDGE,"E0.top");var subQ2=sQuery(id+"F0.wireOp",EDGE,"E0.bottom");var subQ6=sQuery(id+"F0.wireOp",EDGE,"E0.right");Q0=makeQuery(id+"F67.boolean.opBoolean","SPLIT",FACE,{"disambiguationData":[TD([makeQuery(id+"F1.opExtrude","SWEPT_FACE",FACE,{"disambiguationData":[OSD([subQ2])]})])],"derivedFrom":makeQuery(id+"F1.opExtrude","CAP_FACE",FACE,{"disambiguationData":[OSD([subQ2,subQ1,subQ0,subQ6])],"isStart":true})});}
            var sketch = newSketch(context, id + "F90", { "sketchPlane" : qUnion([Q0])});
            skCircle(sketch, "E65", {"center": v(-137.8, 4.46) * mm, "radius": 12.67 * mm});
            skSolve(sketch);
        }
        {
            var Q0;
            Q0=makeQuery(id+"F90.imprint","IMPRINT",FACE,{"disambiguationData":[TD([[makeQuery(id+"F90.imprint","IMPRINT",EDGE,{"derivedFrom":sQuery(id+"F90.wireOp",EDGE,"E65")}),1.0]])]});
            extrude(context, id + "F91", {"entities" : qUnion([Q0]), "operationType" : NewBodyOperationType.ADD, "depth" : 7.62 * mm});
        }
        {
            var Q0;
            Q0=makeQuery(id+"F3.boolean.opBoolean","COPY",FACE,{"derivedFrom":makeQuery(id+"F3.opExtrude","SWEPT_FACE",FACE,{"disambiguationData":[OSD([sQuery(id+"F2.wireOp",EDGE,"E1.right")])]})});
            var sketch = newSketch(context, id + "F92", { "sketchPlane" : qUnion([Q0])});
            skLineSegment(sketch, "E66.bottom", {"start": v(-88.9, 73.3) * mm, "end": v(-55.98, 73.3) * mm});
            skLineSegment(sketch, "E66.top", {"start": v(-88.9, 22.5) * mm, "end": v(-55.98, 22.5) * mm});
            skLineSegment(sketch, "E66.left", {"start": v(-88.9, 73.3) * mm, "end": v(-88.9, 22.5) * mm});
            skLineSegment(sketch, "E66.right", {"start": v(-55.98, 73.3) * mm, "end": v(-55.98, 22.5) * mm});
            skSolve(sketch);
        }
        {
            var Q0;
            Q0 = qSketchRegion(id + "F92", true);
            extrude(context, id + "F93", {"entities" : qUnion([Q0]), "operationType" : NewBodyOperationType.REMOVE, "oppositeDirection" : true, "depth" : 291.85 * mm});
        }
        {
            var Q0;
            Q0=makeQuery(id+"F3.boolean.opBoolean","COPY",FACE,{"derivedFrom":makeQuery(id+"F3.opExtrude","SWEPT_FACE",FACE,{"disambiguationData":[OSD([sQuery(id+"F2.wireOp",EDGE,"E1.right")])]})});
            var sketch = newSketch(context, id + "F94", { "sketchPlane" : qUnion([Q0])});
            skLineSegment(sketch, "E67.bottom", {"start": v(-55.98, 73.3) * mm, "end": v(0, 73.3) * mm});
            skLineSegment(sketch, "E67.top", {"start": v(-55.98, 57.39) * mm, "end": v(0, 57.39) * mm});
            skLineSegment(sketch, "E67.left", {"start": v(-55.98, 73.3) * mm, "end": v(-55.98, 57.39) * mm});
            skLineSegment(sketch, "E67.right", {"start": v(0, 73.3) * mm, "end": v(0, 57.39) * mm});
            skSolve(sketch);
        }
        {
            var Q0;
            Q0 = qSketchRegion(id + "F94", true);
            extrude(context, id + "F95", {"entities" : qUnion([Q0]), "operationType" : NewBodyOperationType.REMOVE, "oppositeDirection" : true, "depth" : 230.38 * mm});
        }
        {
            var Q0;
            Q0=makeQuery(id+"F75.boolean.opBoolean","MERGE",FACE,{"derivedFrom":[makeQuery(id+"F39.boolean.opBoolean","MERGE",FACE,{"derivedFrom":[makeQuery(id+"F13.boolean.opBoolean","COPY",FACE,{"derivedFrom":makeQuery(id+"F13.opExtrude","SWEPT_FACE",FACE,{"disambiguationData":[OSD([sQuery(id+"F12.wireOp",EDGE,"E6.top")])]})}),makeQuery(id+"F39.opExtrude","SWEPT_FACE",FACE,{"disambiguationData":[OSD([sQuery(id+"F38.wireOp",EDGE,"E19.bottom")])]})]}),makeQuery(id+"F75.opExtrude","SWEPT_FACE",FACE,{"disambiguationData":[OSD([sQuery(id+"F74.wireOp",EDGE,"E47.bottom")])]})]});
            var sketch = newSketch(context, id + "F96", { "sketchPlane" : qUnion([Q0])});
            skLineSegment(sketch, "E68.bottom", {"start": v(-175.93, -70.09) * mm, "end": v(-203.87, -70.09) * mm});
            skLineSegment(sketch, "E68.top", {"start": v(-175.93, -30.2) * mm, "end": v(-203.87, -30.2) * mm});
            skLineSegment(sketch, "E68.left", {"start": v(-175.93, -70.09) * mm, "end": v(-175.93, -30.2) * mm});
            skLineSegment(sketch, "E68.right", {"start": v(-203.87, -70.09) * mm, "end": v(-203.87, -30.2) * mm});
            skSolve(sketch);
        }
        {
            var Q0;
            Q0 = qSketchRegion(id + "F96", true);
            extrude(context, id + "F97", {"entities" : qUnion([Q0]), "operationType" : NewBodyOperationType.REMOVE, "oppositeDirection" : true, "depth" : 25.4 * mm});
        }
        {
            var Q0;
            Q0=makeQuery(id+"F85.opExtrude","CAP_FACE",FACE,{"disambiguationData":[OSD([sQuery(id+"F84.wireOp",EDGE,"E59.bottom"),sQuery(id+"F84.wireOp",EDGE,"E59.top"),sQuery(id+"F84.wireOp",EDGE,"E59.left"),sQuery(id+"F84.wireOp",EDGE,"E59.right")])],"isStart":false});
            var sketch = newSketch(context, id + "F98", { "sketchPlane" : qUnion([Q0])});
            skLineSegment(sketch, "E69.bottom", {"start": v(23.63, -14.1) * mm, "end": v(28.47, -14.1) * mm});
            skLineSegment(sketch, "E69.top", {"start": v(23.63, -48.19) * mm, "end": v(28.47, -48.19) * mm});
            skLineSegment(sketch, "E69.left", {"start": v(23.63, -14.1) * mm, "end": v(23.63, -48.19) * mm});
            skLineSegment(sketch, "E69.right", {"start": v(28.47, -14.1) * mm, "end": v(28.47, -48.19) * mm});
            skSolve(sketch);
        }
        {
            var Q0;
            Q0 = qSketchRegion(id + "F98", true);
            extrude(context, id + "F99", {"entities" : qUnion([Q0]), "operationType" : NewBodyOperationType.REMOVE, "oppositeDirection" : true, "depth" : 25.4 * mm});
        }
        {
            var Q0;
            {var subQ0=sQuery(id+"F84.wireOp",EDGE,"E59.left");var subQ1=sQuery(id+"F84.wireOp",EDGE,"E59.top");var subQ2=sQuery(id+"F84.wireOp",EDGE,"E59.bottom");Q0=makeQuery(id+"F99.boolean.opBoolean","SPLIT",FACE,{"disambiguationData":[TD([makeQuery(id+"F85.opExtrude","SWEPT_FACE",FACE,{"disambiguationData":[OSD([subQ0])]})])],"derivedFrom":makeQuery(id+"F85.opExtrude","CAP_FACE",FACE,{"disambiguationData":[OSD([subQ2,subQ1,subQ0,sQuery(id+"F84.wireOp",EDGE,"E59.right")])],"isStart":false})});}
            var sketch = newSketch(context, id + "F100", { "sketchPlane" : qUnion([Q0])});
            skCircle(sketch, "E70", {"center": v(15.96, -24.34) * mm, "radius": 5.48 * mm});
            skSolve(sketch);
        }
        {
            var Q0;
            Q0 = qSketchRegion(id + "F100", true);
            extrude(context, id + "F101", {"entities" : qUnion([Q0]), "operationType" : NewBodyOperationType.ADD, "depth" : 25.4 * mm});
        }
        {
            var Q0;
            Q0=makeQuery(id+"F79.opExtrude","CAP_FACE",FACE,{"disambiguationData":[OSD([sQuery(id+"F78.wireOp",EDGE,"E49")])],"isStart":false});
            var sketch = newSketch(context, id + "F102", { "sketchPlane" : qUnion([Q0])});
            skCircle(sketch, "E71", {"center": v(-121.37, 92.47) * mm, "radius": 15.95 * mm});
            skSolve(sketch);
        }
        {
            var Q0;
            Q0=makeQuery(id+"F102.imprint","IMPRINT",FACE,{"disambiguationData":[TD([[makeQuery(id+"F102.imprint","IMPRINT",EDGE,{"derivedFrom":sQuery(id+"F102.wireOp",EDGE,"E71")}),1.0]])]});
            extrude(context, id + "F103", {"entities" : qUnion([Q0]), "operationType" : NewBodyOperationType.REMOVE, "oppositeDirection" : true, "depth" : 12.7 * mm});
        }
        {
            var Q0;
            Q0=makeQuery(id+"F51.opExtrude","CAP_FACE",FACE,{"disambiguationData":[OSD([sQuery(id+"F50.wireOp",EDGE,"E25")])],"isStart":false});
            var sketch = newSketch(context, id + "F104", { "sketchPlane" : qUnion([Q0])});
            skEllipse(sketch, "E72", {"center": v(32.47, 62.95) * mm, "majorRadius": 20.37 * mm, "minorRadius": 7.54 * mm, "majorAxis": v(0, 1)});
            skSolve(sketch);
        }
        {
            var Q0;
            Q0 = qSketchRegion(id + "F104", true);
            extrude(context, id + "F105", {"entities" : qUnion([Q0]), "operationType" : NewBodyOperationType.REMOVE, "oppositeDirection" : true, "depth" : 12.7 * mm});
        }
        {
            var Q0;
            Q0=makeQuery(id+"F85.boolean.opBoolean","MERGE",FACE,{"derivedFrom":[makeQuery(id+"F1.opExtrude","SWEPT_FACE",FACE,{"disambiguationData":[OSD([sQuery(id+"F0.wireOp",EDGE,"E0.top")])]}),makeQuery(id+"F85.opExtrude","SWEPT_FACE",FACE,{"disambiguationData":[OSD([sQuery(id+"F84.wireOp",EDGE,"E59.top")])]})]});
            var sketch = newSketch(context, id + "F106", { "sketchPlane" : qUnion([Q0])});
            skLineSegment(sketch, "E73.bottom", {"start": v(-50.08, 15.42) * mm, "end": v(-57.97, 15.42) * mm});
            skLineSegment(sketch, "E73.top", {"start": v(-50.08, 24.33) * mm, "end": v(-57.97, 24.33) * mm});
            skLineSegment(sketch, "E73.left", {"start": v(-50.08, 15.42) * mm, "end": v(-50.08, 24.33) * mm});
            skLineSegment(sketch, "E73.right", {"start": v(-57.97, 15.42) * mm, "end": v(-57.97, 24.33) * mm});
            skLineSegment(sketch, "E74.bottom", {"start": v(-44.38, 46.66) * mm, "end": v(-52.54, 46.66) * mm});
            skLineSegment(sketch, "E74.top", {"start": v(-44.38, 56.58) * mm, "end": v(-52.54, 56.58) * mm});
            skLineSegment(sketch, "E74.left", {"start": v(-44.38, 46.66) * mm, "end": v(-44.38, 56.58) * mm});
            skLineSegment(sketch, "E74.right", {"start": v(-52.54, 46.66) * mm, "end": v(-52.54, 56.58) * mm});
            skSolve(sketch);
        }
        {
            var Q0;
            Q0 = qSketchRegion(id + "F106", true);
            extrude(context, id + "F107", {"entities" : qUnion([Q0]), "operationType" : NewBodyOperationType.ADD, "depth" : 12.7 * mm});
        }
        {
            var Q0;
            {var subQ0=sQuery(id+"F74.wireOp",EDGE,"E47.right");var subQ1=sQuery(id+"F74.wireOp",EDGE,"E47.top");Q0=makeQuery(id+"F81.boolean.opBoolean","SPLIT",FACE,{"disambiguationData":[TD([makeQuery(id+"F75.opExtrude","SWEPT_FACE",FACE,{"disambiguationData":[OSD([subQ0])]})])],"derivedFrom":makeQuery(id+"F77.boolean.opBoolean","MERGE",FACE,{"derivedFrom":[makeQuery(id+"F75.opExtrude","CAP_FACE",FACE,{"disambiguationData":[OSD([sQuery(id+"F74.wireOp",EDGE,"E47.bottom"),subQ1,sQuery(id+"F74.wireOp",EDGE,"E47.left"),subQ0])],"isStart":true}),makeQuery(id+"F77.opExtrude","SWEPT_FACE",FACE,{"disambiguationData":[OSD([sQuery(id+"F76.wireOp",EDGE,"E48.left")])]})]})});}
            var sketch = newSketch(context, id + "F108", { "sketchPlane" : qUnion([Q0])});
            skEllipse(sketch, "E75", {"center": v(-109.63, 20.1) * mm, "majorRadius": 22.28 * mm, "minorRadius": 13.66 * mm, "majorAxis": v(-0.68, 0.74)});
            skSolve(sketch);
        }
        {
            var Q0;
            Q0 = qSketchRegion(id + "F108", true);
            extrude(context, id + "F109", {"entities" : qUnion([Q0]), "operationType" : NewBodyOperationType.ADD, "depth" : 12.7 * mm});
        }
    });
